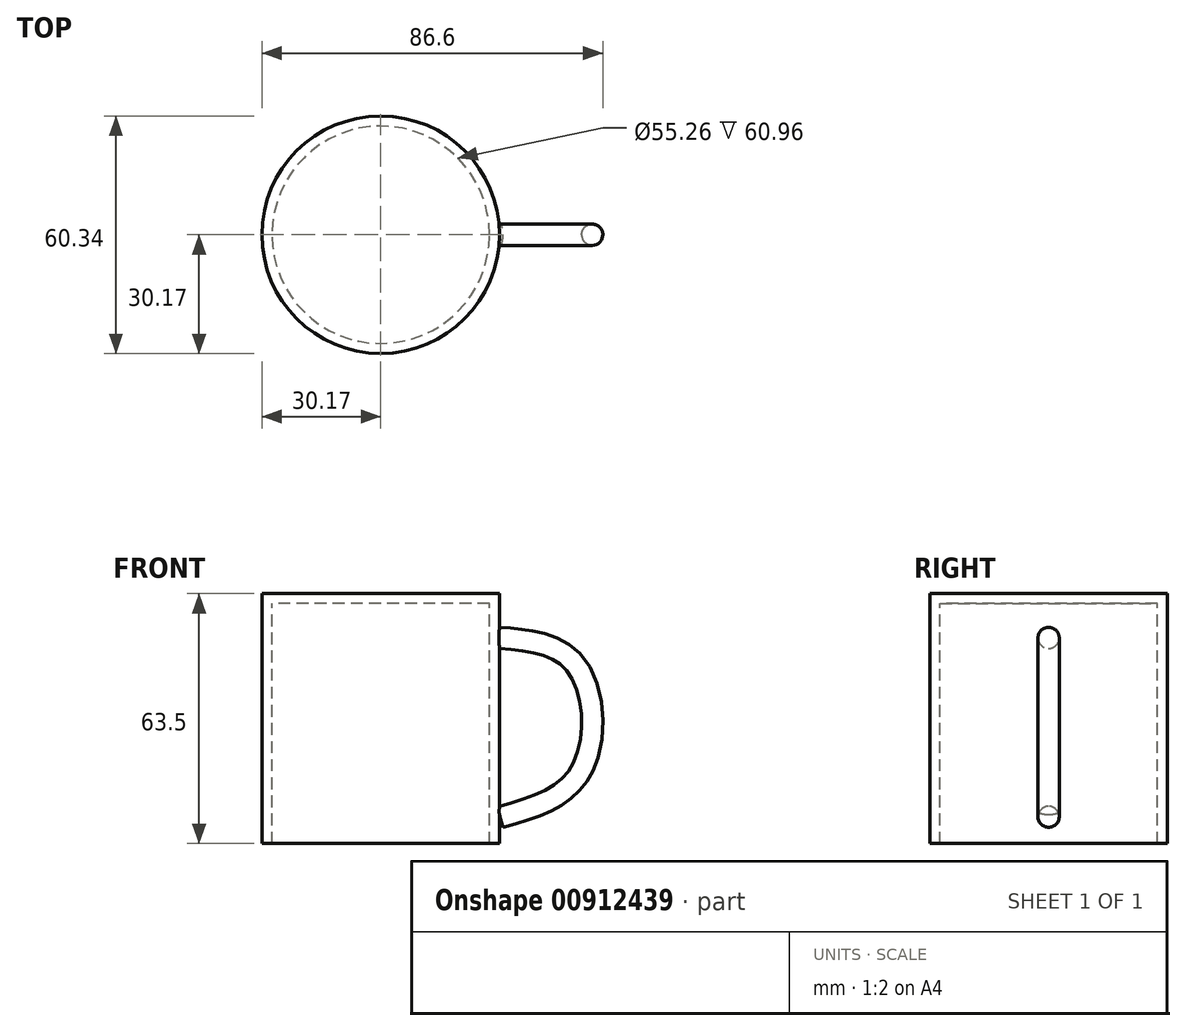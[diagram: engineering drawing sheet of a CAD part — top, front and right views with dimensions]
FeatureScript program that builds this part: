
annotation { "Feature Type Name" : "Feature", "Feature Type Description" : "" }
export const myFeature = defineFeature(function(context is Context, id is Id, definition is map)
    precondition{}
    {
        {
            var Q0;
            Q0=qCreatedBy(makeId("Top.planeOp"),FACE);
            var sketch = newSketch(context, id + "F0", { "sketchPlane" : qUnion([Q0])});
            skCircle(sketch, "E0", {"center": v(0, 0) * mm, "radius": 30.17 * mm});
            skSolve(sketch);
        }
        {
            var Q0;
            Q0=makeQuery(id+"F0.imprint","IMPRINT",FACE,{"disambiguationData":[TD([[makeQuery(id+"F0.imprint","IMPRINT",EDGE,{"derivedFrom":sQuery(id+"F0.wireOp",EDGE,"E0")}),1.0]])]});
            extrude(context, id + "F1", {"entities" : qUnion([Q0]), "oppositeDirection" : true, "depth" : 63.5 * mm, "offsetDistance" : 25.4 * mm});
        }
        {
            var Q0;
            Q0=makeQuery(id+"F1.opExtrude","CAP_FACE",FACE,{"disambiguationData":[OSD([sQuery(id+"F0.wireOp",EDGE,"E0")])],"isStart":false});
            shell(context, id + "F2", {"entities" : qUnion([Q0]), "thickness" : 2.54 * mm});
        }
        {
            var Q0;
            Q0=qCreatedBy(makeId("Front.planeOp"),FACE);
            var sketch = newSketch(context, id + "F3", { "sketchPlane" : qUnion([Q0])});
            skFitSpline(sketch, "E1", {"points": [v(30.33, -56.69) * mm, v(50.79, -45.07) * mm, v(49.31, -17.97) * mm, v(29.4, -11.3) * mm], "startDerivative": vector(74.03, 20.33) * mm, "endDerivative": vector(-70.13, 5.17) * mm});
            skSolve(sketch);
        }
        {
            var Q0;
            Q0=sQuery(id+"F3.wireOp",EDGE,"E1");
            var Q1;
            Q1=sQuery(id+"F3.wireOp",VERTEX,"E1.end");
            cPlane(context, id + "F4", {"entities" : qUnion([Q0, Q1]), "cplaneType" : CPlaneType.CURVE_POINT, "offset" : 25.4 * mm, "width" : 152.4 * mm, "height" : 152.4 * mm});
        }
        {
            var Q0;
            Q0=qCreatedBy(id+"F4.planeOp",FACE);
            var sketch = newSketch(context, id + "F5", { "sketchPlane" : qUnion([Q0])});
            skCircle(sketch, "E2", {"center": v(0, -9.02) * mm, "radius": 2.7 * mm});
            skSolve(sketch);
        }
        {
            var Q0;
            Q0 = qSketchRegion(id + "F5", true);
            var Q1;
            Q1=sQuery(id+"F3.wireOp",EDGE,"E1");
            sweep(context, id + "F6", {"operationType" : NewBodyOperationType.ADD, "profiles" : qUnion([Q0]), "path" : qUnion([Q1])});
        }
    });
